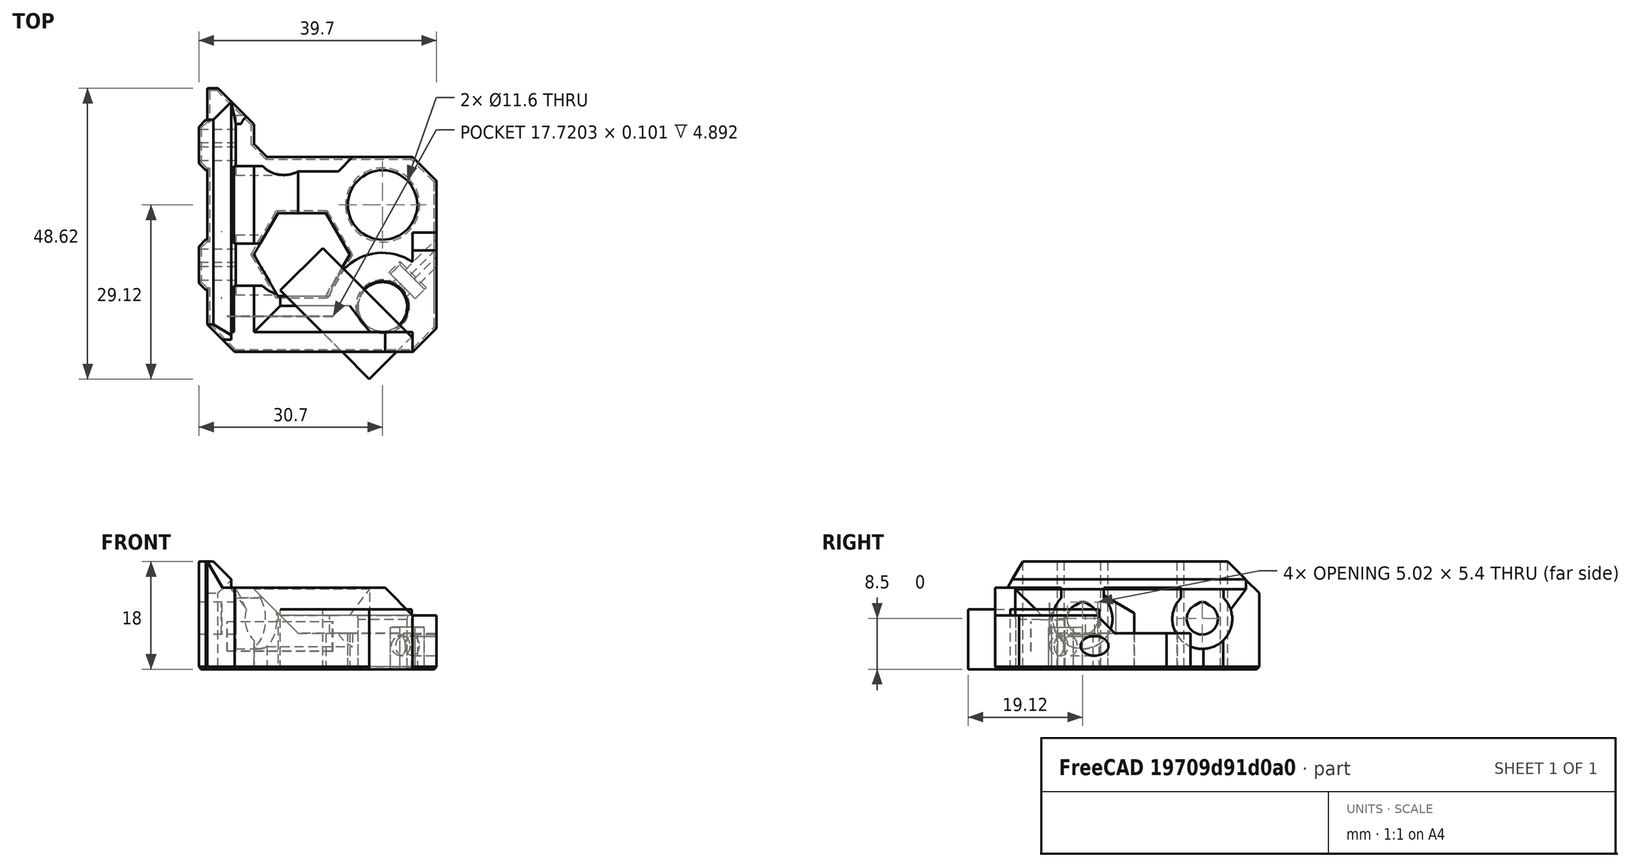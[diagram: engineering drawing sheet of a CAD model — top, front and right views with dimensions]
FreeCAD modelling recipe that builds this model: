
FCSTD DOCUMENT  (FreeCAD 0.18R14555 (Git shallow))
Label: bear-ztop-2.1-through
License: All rights reserved
LicenseURL: http://en.wikipedia.org/wiki/All_rights_reserved
objects: Part::Cut×6, Part::Cylinder×5, Part::Chamfer×5, Part::Feature×4, Part::Box×4, Part::MultiFuse×4
note: 28 computed .brp shape members not serialized (recipe doc carries the construction recipe); baked Part::Feature solids carry a one-line shape summary decoded from their .brp

FEATURE [Part::Feature] Part__Feature  label="z_top v1"
  Placement = pos=(0,0,6) rot=(0,0,1;0rad)
  shape: bbox 39.72 x 44.11 x 18.02 mm, 127 faces (baked)
FEATURE [Part::Feature] Box001001  label="angle-nut"
  Placement = pos=(3.39411,3.39411,0) rot=(0,0,1;0.785398rad)
  shape: bbox 5.657 x 5.657 x 6 mm, 6 faces (baked)
FEATURE [Part::Cylinder] Cylinder
  Angle = 360
  AttacherType = Attacher::AttachEngine3D
  Height = 23
  Placement = pos=(0,2e-15,3.9) rot=(-0.862856,0.357407,-0.357407;1.71777rad)
  Radius = 1.65
FEATURE [Part::Box] Box  label="Cube"
  AttacherType = Attacher::AttachEngine3D
  Height = 9
  Length = 4
  Placement = pos=(5,-7.59,0) rot=(0,0,1;0rad)
  Width = 20
FEATURE [Part::Box] Box001002  label="Cube001"
  AttacherType = Attacher::AttachEngine3D
  Height = 9
  Length = 5
  Placement = pos=(5,-17.59,0) rot=(0,0,1;0rad)
  Width = 5
FEATURE [Part::Chamfer] Chamfer
  Base = -> Box001002
  Edges = 1 edges r=4: [Edge3]
  Placement = pos=(0,9,0) rot=(0,0,1;0rad)
FEATURE [Part::Cut] Cut
  Base = -> Box
  Tool = -> Chamfer
FEATURE [Part::Chamfer] Chamfer001  label="adt-1"
  Base = -> Cut
  Edges = 1 edges r=3: [Edge8]
FEATURE [Part::Cylinder] Cylinder001
  Angle = 360
  AttacherType = Attacher::AttachEngine3D
  Height = 9
  Radius = 9
FEATURE [Part::Cylinder] Cylinder002
  Angle = 360
  AttacherType = Attacher::AttachEngine3D
  Height = 9
  Radius = 6
FEATURE [Part::Cut] Cut001
  Base = -> Cylinder001
  Tool = -> Cylinder002
FEATURE [Part::Box] Box001003  label="Cube002"
  AttacherType = Attacher::AttachEngine3D
  Height = 10
  Length = 10
  Placement = pos=(-2.22183,-12.1213,0) rot=(0,0,1;0.785398rad)
  Width = 21
FEATURE [Part::Box] Box001004  label="Cube003"
  AttacherType = Attacher::AttachEngine3D
  Height = 10
  Length = 21
  Placement = pos=(-10,-10,0) rot=(0,0,1;0rad)
  Width = 10
FEATURE [Part::Cut] Cut002  label="adt-2"
  Base = -> Cut001
  Tool = -> Box001004
FEATURE [Part::Cylinder] Cylinder003
  Angle = 360
  AttacherType = Attacher::AttachEngine3D
  Height = 23
  Placement = pos=(0,4e-15,5.3) rot=(-0.862856,0.357407,-0.357407;1.71777rad)
  Radius = 0.5
FEATURE [Part::Cylinder] Cylinder004  label="enlarger-shaft-slot"
  Angle = 360
  AttacherType = Attacher::AttachEngine3D
  Height = 10
  Radius = 4.1
FEATURE [Part::MultiFuse] Fusion003  label="set-screw-slot"
  Shapes = -> [Cylinder003,Cylinder]
FEATURE [Part::Chamfer] Chamfer002
  Base = -> Cut002
  Edges = 1 edges r=0.4: [Edge3]
FEATURE [Part::Chamfer] Chamfer003
  Base = -> Chamfer001
  Edges = 2 edges r=0.4: [Edge11,Edge15]
FEATURE [Part::MultiFuse] Fusion  label="adt"
  Shapes = -> [Chamfer002,Chamfer003]
FEATURE [Part::MultiFuse] Fusion004
  Shapes = -> [Part__Feature,Fusion]
FEATURE [Part::Feature] Box001005  label="angle-nut001"
  Placement = pos=(3.39411,3.39411,1) rot=(0,0,1;0.785398rad)
  shape: bbox 5.657 x 5.657 x 6 mm, 6 faces (baked)
FEATURE [Part::MultiFuse] Fusion005  label="square-nut-slot"
  Shapes = -> [Box001005,Box001001]
FEATURE [Part::Cut] Cut003
  Base = -> Fusion004
  Tool = -> Fusion005
FEATURE [Part::Cut] Cut004
  Base = -> Cut003
  Tool = -> Fusion003
FEATURE [Part::Cut] Cut005
  Base = -> Cut004
  Tool = -> Cylinder004
FEATURE [Part::Feature] Cut005001  label="Cut006"
  shape: bbox 42.06 x 44.11 x 18.02 mm, 134 faces (baked)
FEATURE [Part::Chamfer] Chamfer004
  Base = -> Cut005001
  Edges = 5 edges r=0.4: [Edge168,Edge169,Edge270,Edge292,Edge293]
